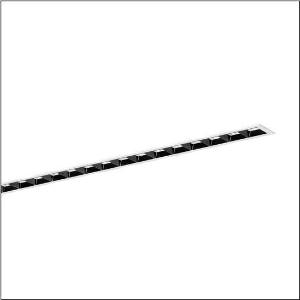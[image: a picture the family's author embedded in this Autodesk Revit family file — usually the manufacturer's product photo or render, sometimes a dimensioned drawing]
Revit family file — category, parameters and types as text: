
# Revit family: silica_r__21_51mx11tctaw_2435
name_source: partatom
category: Lighting Fixtures
units: mm (PartAtom-declared; Revit-internal decimal feet)

## family parameters
Cut with Voids When Loaded = No
Host = Face
Light Source = No
Part Type = Normal
Room Calculation Point = No
Round Connector Dimension = Use Diameter
Shared = No

## types (1)
- --- (1 x LED, 9300 lm, 80.5 W, 6500K)
    Apparent Load = 81 VA
    CIE Flux Codes = 85 99 100 100 100
    Color Rendering = 80
    Color Temperature = 6500K
    Default Elevation = 1800 mm
    Description = Silica® 21, office luminaire, primary light control with darklight reflector, of PMMA, black, CAT 2 (L<= 3000cd/m²), light emission: direct distribution, primary light characteristic: symmetric, installation type: recessed, LED, rated luminous flux: 9.300lm, luminous efficacy: 110lm/W, light colour: 8tw, colour temperature: 2700..6500K, with terminal, 3+2-pole, max. 2.5mm², mains connection: 220..240V, AC, 50/60Hz, rated input power: 84.6W, luminaire housing, of aluminium, traffic white (RAL 9016), length: 3.028mm, width: 79mm, height: 53mm, protection rating (complete): IP20, insulation class (complete): insulation class I (protective earthing), certification: CE, permissible operating ambient temperature: 0..+35°C, standard: EN 50419, packaging unit: 1 piece
    Height = 0 mm  [stored 0 ft]
    Lamp = 1 x LED
    Lamp Light Flux = 9300 lm
    Lamp Power = 80.5 W
    Lamp count = 1
    Length = 3027 mm
    Luminous efficacy = 116 lm/W
    Manufacturer = Siteco
    ModVariant = No
    Model = 51MX11TCTAW
    Mounting Place = Ceiling
    Mounting Type = Recessed
    Number of Poles = 1
    OnlyDefault = Yes
    Power Factor = 1
    Product Name = Silica® 21
    Product group = office luminaire | ceiling recessed
    ProductGroupID = 401
    Protection Class = Protection class I
    Protection Degree = IP 20
    RLX_Detail_Level = 1
    RLX_Emergency_Light_Flux = 0 lm
    RLX_Emergency_Type = 0
    RLX_Emergency_Type_DB = No
    RlxData = <blob elided: 59937 chars, md5=045bd610>
    Socket = socket
    Standby Power = 0 W
    System Light Flux = 9300 lm
    System Power = 81 W
    Type Comments = individual setting
    Type Image = l_1313610.jpg
    URL = http://relux.com
    VarID = @adj_089463
    Voltage = 0 V
    Weight = 0.00 kg
    Width = 79 mm

note: [stored X ft] marks values corroborated as IEEE doubles in the binary element streams (Revit-internal decimal feet)

## geometry (parser evidence)
native form markers: Blend x4, Sweep x12
no freeform markers — native parametric forms only
